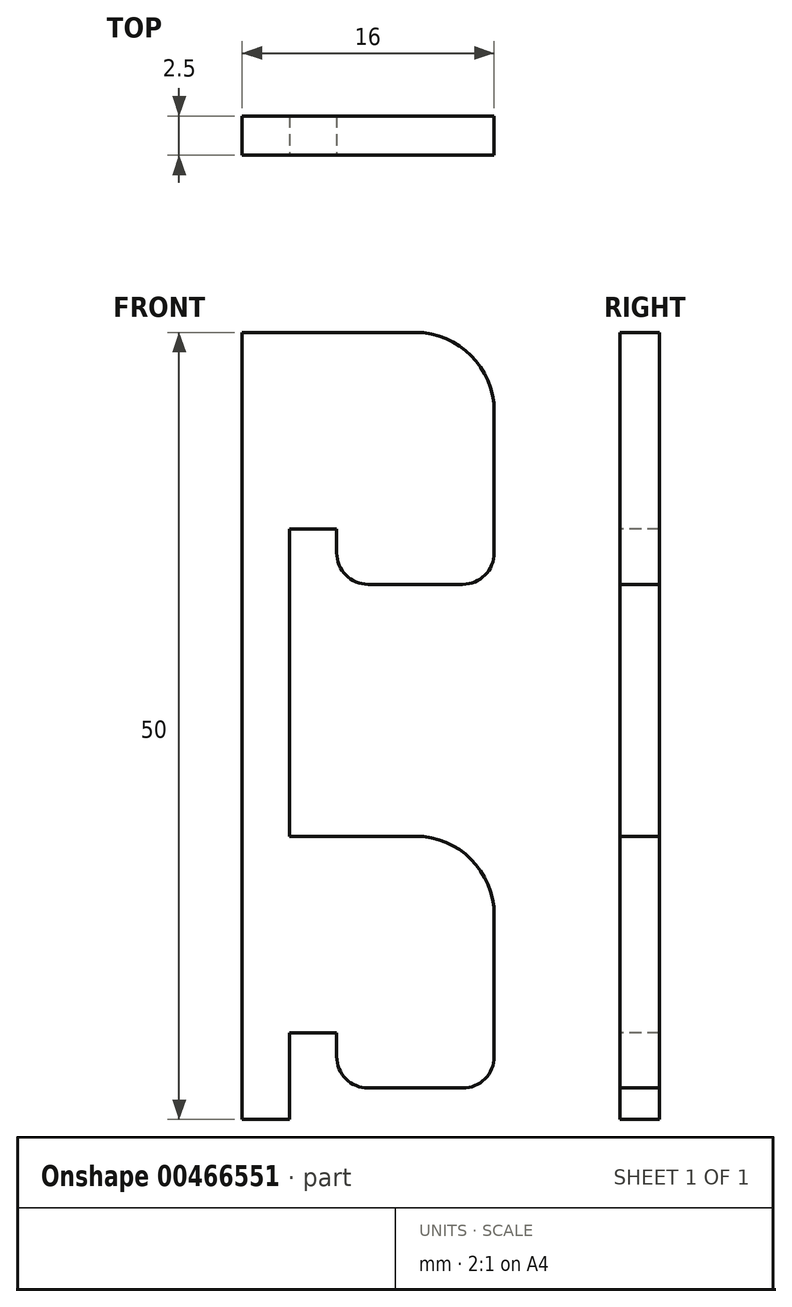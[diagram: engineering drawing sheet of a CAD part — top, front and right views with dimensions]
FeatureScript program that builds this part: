
annotation { "Feature Type Name" : "Feature", "Feature Type Description" : "" }
export const myFeature = defineFeature(function(context is Context, id is Id, definition is map)
    precondition{}
    {
        {
            assignVariable(context, id + "F0", {"name" : "Width", "anyValue" : 2.5});
        }
        {
            var Q0;
            Q0=qCreatedBy(makeId("Front.planeOp"),FACE);
            var sketch = newSketch(context, id + "F1", { "sketchPlane" : qUnion([Q0])});
            skLineSegment(sketch, "E0.bottom", {"start": v(0, 50) * mm, "end": v(3, 50) * mm});
            skLineSegment(sketch, "E0.top", {"start": v(0, 0) * mm, "end": v(3, 0) * mm});
            skLineSegment(sketch, "E0.left", {"start": v(0, 50) * mm, "end": v(0, 0) * mm});
            skLineSegment(sketch, "E0.right", {"start": v(3, 50) * mm, "end": v(3, 0) * mm});
            skLineSegment(sketch, "E1.bottom", {"start": v(3, 50) * mm, "end": v(6, 50) * mm});
            skLineSegment(sketch, "E1.top", {"start": v(3, 37.5) * mm, "end": v(6, 37.5) * mm});
            skLineSegment(sketch, "E1.left", {"start": v(3, 50) * mm, "end": v(3, 37.5) * mm});
            skLineSegment(sketch, "E1.right", {"start": v(6, 50) * mm, "end": v(6, 37.5) * mm});
            skLineSegment(sketch, "E2.bottom", {"start": v(3, 5.5) * mm, "end": v(6, 5.5) * mm});
            skLineSegment(sketch, "E2.top", {"start": v(3, 18) * mm, "end": v(6, 18) * mm});
            skLineSegment(sketch, "E2.left", {"start": v(3, 18) * mm, "end": v(3, 5.5) * mm});
            skLineSegment(sketch, "E2.right", {"start": v(6, 18) * mm, "end": v(6, 5.5) * mm});
            skLineSegment(sketch, "E3.bottom", {"start": v(6, 50) * mm, "end": v(11, 50) * mm});
            skLineSegment(sketch, "E3.top", {"start": v(8, 34) * mm, "end": v(14, 34) * mm});
            skLineSegment(sketch, "E3.left", {"start": v(6, 50) * mm, "end": v(6, 36) * mm});
            skLineSegment(sketch, "E3.right", {"start": v(16, 45) * mm, "end": v(16, 36) * mm});
            skLineSegment(sketch, "E4.bottom", {"start": v(6, 18) * mm, "end": v(11, 18) * mm});
            skLineSegment(sketch, "E4.top", {"start": v(8, 2) * mm, "end": v(14, 2) * mm});
            skLineSegment(sketch, "E4.left", {"start": v(6, 18) * mm, "end": v(6, 4) * mm});
            skLineSegment(sketch, "E4.right", {"start": v(16, 13) * mm, "end": v(16, 4) * mm});
            skPoint(sketch, "E5.visualSharp", {"position": v(16, 50) * mm});
            skArc(sketch, "E5.filletArc", {"start": v(16, 45) * mm, "mid": v(14.54, 48.54) * mm, "end": v(11, 50) * mm});
            skPoint(sketch, "E6.visualSharp", {"position": v(16, 18) * mm});
            skArc(sketch, "E6.filletArc", {"start": v(16, 13) * mm, "mid": v(14.54, 16.54) * mm, "end": v(11, 18) * mm});
            skPoint(sketch, "E7.visualSharp", {"position": v(16, 2) * mm});
            skArc(sketch, "E7.filletArc", {"start": v(14, 2) * mm, "mid": v(15.41, 2.59) * mm, "end": v(16, 4) * mm});
            skPoint(sketch, "E8.visualSharp", {"position": v(6, 2) * mm});
            skArc(sketch, "E8.filletArc", {"start": v(6, 4) * mm, "mid": v(6.59, 2.59) * mm, "end": v(8, 2) * mm});
            skPoint(sketch, "E9.visualSharp", {"position": v(16, 34) * mm});
            skArc(sketch, "E9.filletArc", {"start": v(14, 34) * mm, "mid": v(15.41, 34.59) * mm, "end": v(16, 36) * mm});
            skPoint(sketch, "E10.visualSharp", {"position": v(6, 34) * mm});
            skArc(sketch, "E10.filletArc", {"start": v(6, 36) * mm, "mid": v(6.59, 34.59) * mm, "end": v(8, 34) * mm});
            skSolve(sketch);
        }
        {
            var Q0;
            Q0 = qSketchRegion(id + "F1", true);
            extrude(context, id + "F2", {"entities" : qUnion([Q0]), "endBound" : BoundingType.SYMMETRIC, "oppositeDirection" : true, "depth" : (getVariable(context, 'Width')) * mm});
        }
    });
